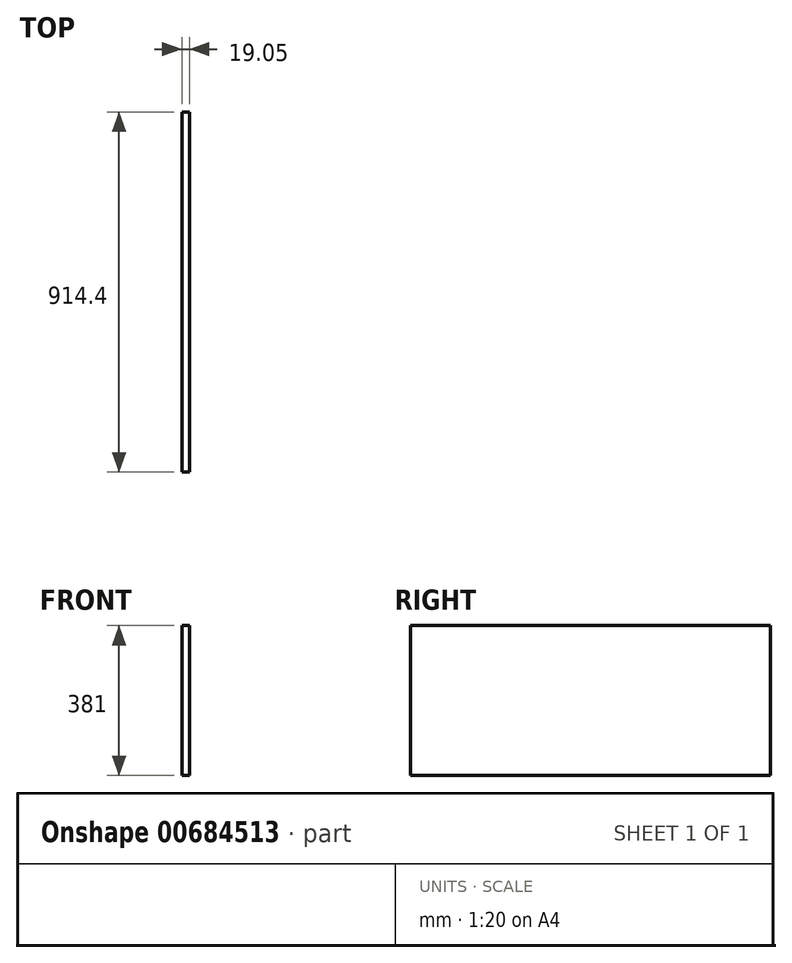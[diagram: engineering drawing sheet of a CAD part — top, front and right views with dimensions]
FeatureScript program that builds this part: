
annotation { "Feature Type Name" : "Feature", "Feature Type Description" : "" }
export const myFeature = defineFeature(function(context is Context, id is Id, definition is map)
    precondition{}
    {
        {
            var Q0;
            Q0=qCreatedBy(makeId("Right.planeOp"),FACE);
            var sketch = newSketch(context, id + "F0", { "sketchPlane" : qUnion([Q0])});
            skLineSegment(sketch, "E0.bottom", {"start": v(-222.21, 216.33) * mm, "end": v(692.19, 216.33) * mm});
            skLineSegment(sketch, "E0.top", {"start": v(-222.21, -164.67) * mm, "end": v(692.19, -164.67) * mm});
            skLineSegment(sketch, "E0.left", {"start": v(-222.21, 216.33) * mm, "end": v(-222.21, -164.67) * mm});
            skLineSegment(sketch, "E0.right", {"start": v(692.19, 216.33) * mm, "end": v(692.19, -164.67) * mm});
            skSolve(sketch);
        }
        {
            var Q0;
            Q0=makeQuery(id+"F0.imprint","IMPRINT",FACE,{"disambiguationData":[TD([[makeQuery(id+"F0.imprint","IMPRINT",EDGE,{"derivedFrom":sQuery(id+"F0.wireOp",EDGE,"E0.bottom")}),-1.0]])]});
            extrude(context, id + "F1", {"entities" : qUnion([Q0]), "depth" : 19.05 * mm, "offsetDistance" : 25.4 * mm});
        }
    });
